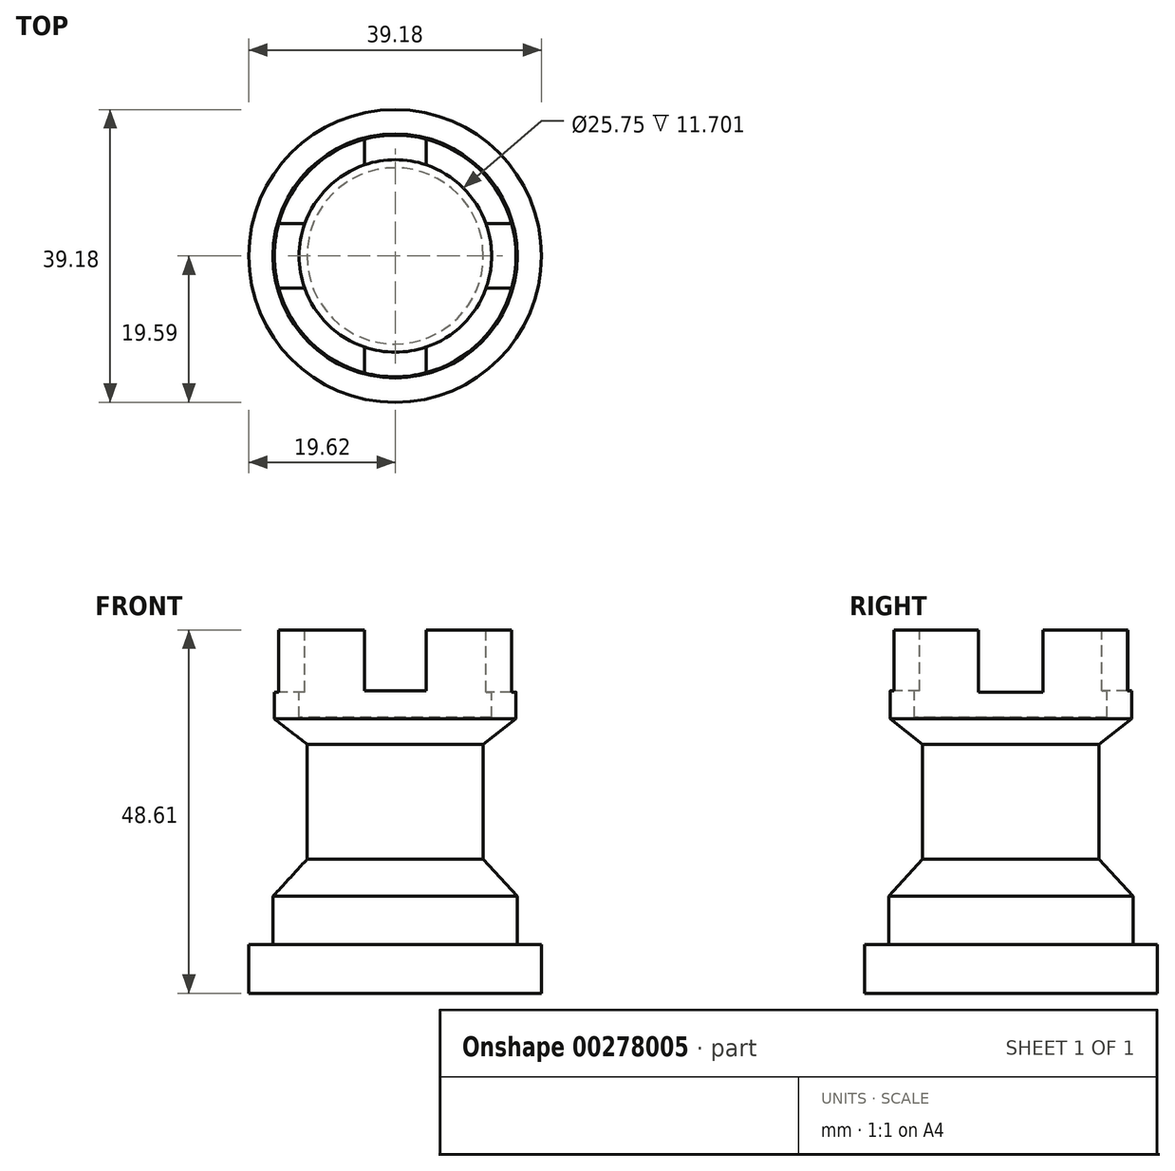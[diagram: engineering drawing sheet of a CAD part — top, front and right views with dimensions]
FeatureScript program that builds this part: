
annotation { "Feature Type Name" : "Feature", "Feature Type Description" : "" }
export const myFeature = defineFeature(function(context is Context, id is Id, definition is map)
    precondition{}
    {
        {
            var Q0;
            Q0=qCreatedBy(makeId("Front.planeOp"),FACE);
            var sketch = newSketch(context, id + "F0", { "sketchPlane" : qUnion([Q0])});
            skLineSegment(sketch, "E0", {"start": v(-34.6, -2.11) * mm, "end": v(-15.02, -2.11) * mm});
            skLineSegment(sketch, "E1", {"start": v(-15.02, -2.11) * mm, "end": v(-15.02, 46.5) * mm});
            skLineSegment(sketch, "E2", {"start": v(-34.6, -2.11) * mm, "end": v(-34.6, 4.43) * mm});
            skLineSegment(sketch, "E3", {"start": v(-34.6, 4.43) * mm, "end": v(-31.37, 4.43) * mm});
            skLineSegment(sketch, "E4", {"start": v(-31.37, 4.43) * mm, "end": v(-31.37, 10.86) * mm});
            skLineSegment(sketch, "E5", {"start": v(-31.37, 10.86) * mm, "end": v(-26.81, 15.82) * mm});
            skLineSegment(sketch, "E6", {"start": v(-26.81, 15.82) * mm, "end": v(-26.81, 31.21) * mm});
            skLineSegment(sketch, "E7", {"start": v(-26.81, 31.21) * mm, "end": v(-31.18, 34.62) * mm});
            skLineSegment(sketch, "E8", {"start": v(-31.18, 34.62) * mm, "end": v(-31.18, 46.5) * mm});
            skLineSegment(sketch, "E9", {"start": v(-31.18, 46.5) * mm, "end": v(-24.66, 46.5) * mm});
            skLineSegment(sketch, "E10", {"start": v(-24.66, 46.5) * mm, "end": v(-24.66, 42.83) * mm});
            skLineSegment(sketch, "E11", {"start": v(-24.66, 42.83) * mm, "end": v(-20.43, 42.83) * mm});
            skLineSegment(sketch, "E12", {"start": v(-20.43, 42.83) * mm, "end": v(-20.43, 46.5) * mm});
            skLineSegment(sketch, "E13", {"start": v(-20.43, 46.5) * mm, "end": v(-15.02, 46.5) * mm});
            skSolve(sketch);
        }
        {
            var Q0;
            Q0=makeQuery(id+"F0.imprint","IMPRINT",FACE,{"disambiguationData":[TD([[makeQuery(id+"F0.imprint","IMPRINT",EDGE,{"derivedFrom":sQuery(id+"F0.wireOp",EDGE,"E0")}),1.0]])]});
            var Q1;
            Q1=sQuery(id+"F0.wireOp",EDGE,"E1");
            revolve(context, id + "F1", {"entities" : qUnion([Q0]), "axis" : qUnion([Q1]), "revolveType" : RevolveType.FULL});
        }
        {
            var Q0;
            Q0=makeQuery(id+"F1.opRevolve","SWEPT_BODY",BODY,{"disambiguationData":[OSD([sQuery(id+"F0.wireOp",EDGE,"E0"),sQuery(id+"F0.wireOp",EDGE,"E1"),sQuery(id+"F0.wireOp",EDGE,"E2"),sQuery(id+"F0.wireOp",EDGE,"E3"),sQuery(id+"F0.wireOp",EDGE,"E4"),sQuery(id+"F0.wireOp",EDGE,"E5"),sQuery(id+"F0.wireOp",EDGE,"E6"),sQuery(id+"F0.wireOp",EDGE,"E7"),sQuery(id+"F0.wireOp",EDGE,"E8"),sQuery(id+"F0.wireOp",EDGE,"E9"),sQuery(id+"F0.wireOp",EDGE,"E10"),sQuery(id+"F0.wireOp",EDGE,"E11"),sQuery(id+"F0.wireOp",EDGE,"E12"),sQuery(id+"F0.wireOp",EDGE,"E13")])]});
            transform(context, id + "F2", {"entities" : qUnion([Q0]), "transformType" : TransformType.TRANSLATION_3D, "dx" : 15 * mm, "dy" : 0 * mm, "dz" : 2.03 * mm, "makeCopy" : false});
        }
        {
            var Q0;
            Q0=qCreatedBy(makeId("Top.planeOp"),FACE);
            cPlane(context, id + "F3", {"entities" : qUnion([Q0]), "cplaneType" : CPlaneType.OFFSET, "offset" : 49.53 * mm, "width" : 152.4 * mm, "height" : 152.4 * mm});
        }
        {
            var Q0;
            Q0=qCreatedBy(id+"F3.planeOp",FACE);
            var sketch = newSketch(context, id + "F4", { "sketchPlane" : qUnion([Q0])});
            skCircle(sketch, "E14", {"center": v(0, 0) * mm, "radius": 12.88 * mm});
            skSolve(sketch);
        }
        {
            var Q0;
            Q0 = qSketchRegion(id + "F4", true);
            extrude(context, id + "F5", {"entities" : qUnion([Q0]), "operationType" : NewBodyOperationType.REMOVE, "oppositeDirection" : true, "depth" : 12.7 * mm});
        }
        {
            var Q0;
            Q0=qCreatedBy(makeId("Front.planeOp"),FACE);
            var sketch = newSketch(context, id + "F6", { "sketchPlane" : qUnion([Q0])});
            skLineSegment(sketch, "E15.bottom", {"start": v(4.11, 58.95) * mm, "end": v(-4.11, 58.95) * mm});
            skLineSegment(sketch, "E15.top", {"start": v(4.11, 40.4) * mm, "end": v(-4.11, 40.4) * mm});
            skLineSegment(sketch, "E15.left", {"start": v(4.11, 58.95) * mm, "end": v(4.11, 40.4) * mm});
            skLineSegment(sketch, "E15.right", {"start": v(-4.11, 58.95) * mm, "end": v(-4.11, 40.4) * mm});
            skPoint(sketch, "E15.middle", {"position": v(0, 49.67) * mm});
            skSolve(sketch);
        }
        {
            var Q0;
            Q0 = qSketchRegion(id + "F6", true);
            extrude(context, id + "F7", {"entities" : qUnion([Q0]), "operationType" : NewBodyOperationType.REMOVE, "endBound" : BoundingType.SYMMETRIC, "oppositeDirection" : true, "depth" : 50.8 * mm});
        }
        {
            var Q0;
            Q0=qCreatedBy(makeId("Right.planeOp"),FACE);
            var sketch = newSketch(context, id + "F8", { "sketchPlane" : qUnion([Q0])});
            skLineSegment(sketch, "E16.bottom", {"start": v(4.31, 58.8) * mm, "end": v(-4.31, 58.8) * mm});
            skLineSegment(sketch, "E16.top", {"start": v(4.31, 40.25) * mm, "end": v(-4.31, 40.25) * mm});
            skLineSegment(sketch, "E16.left", {"start": v(4.31, 58.8) * mm, "end": v(4.31, 40.25) * mm});
            skLineSegment(sketch, "E16.right", {"start": v(-4.31, 58.8) * mm, "end": v(-4.31, 40.25) * mm});
            skPoint(sketch, "E16.middle", {"position": v(0, 49.53) * mm});
            skSolve(sketch);
        }
        {
            var Q0;
            Q0 = qSketchRegion(id + "F8", true);
            extrude(context, id + "F9", {"entities" : qUnion([Q0]), "operationType" : NewBodyOperationType.REMOVE, "endBound" : BoundingType.SYMMETRIC, "depth" : 50.8 * mm});
        }
    });
